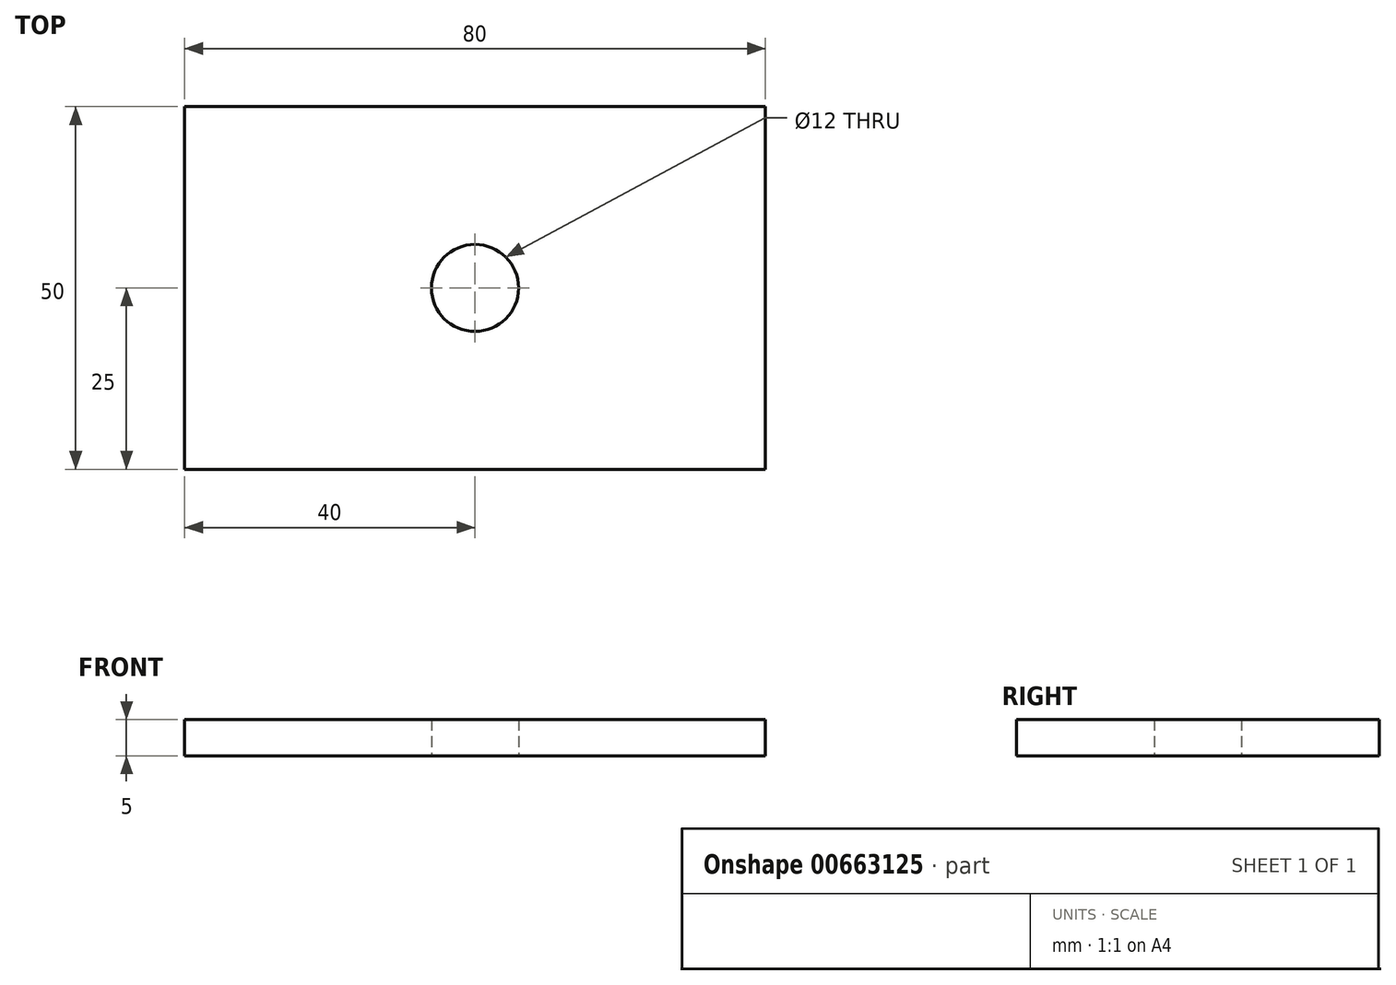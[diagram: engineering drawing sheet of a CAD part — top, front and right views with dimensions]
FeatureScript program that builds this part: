
annotation { "Feature Type Name" : "Feature", "Feature Type Description" : "" }
export const myFeature = defineFeature(function(context is Context, id is Id, definition is map)
    precondition{}
    {
        {
            var Q0;
            Q0=qCreatedBy(makeId("Top.planeOp"),FACE);
            var sketch = newSketch(context, id + "F0", { "sketchPlane" : qUnion([Q0])});
            skLineSegment(sketch, "E0.bottom", {"start": v(0, 0) * mm, "end": v(80, 0) * mm});
            skLineSegment(sketch, "E0.top", {"start": v(0, 50) * mm, "end": v(80, 50) * mm});
            skLineSegment(sketch, "E0.left", {"start": v(0, 0) * mm, "end": v(0, 50) * mm});
            skLineSegment(sketch, "E0.right", {"start": v(80, 0) * mm, "end": v(80, 50) * mm});
            skPoint(sketch, "E0.middle", {"position": v(40, 25) * mm});
            skCircle(sketch, "E1", {"center": v(40, 25) * mm, "radius": 6 * mm});
            skSolve(sketch);
        }
        {
            var Q0;
            Q0 = qSketchRegion(id + "F0", true);
            extrude(context, id + "F1", {"entities" : qUnion([Q0]), "depth" : 5 * mm, "offsetDistance" : 25 * mm});
        }
    });
